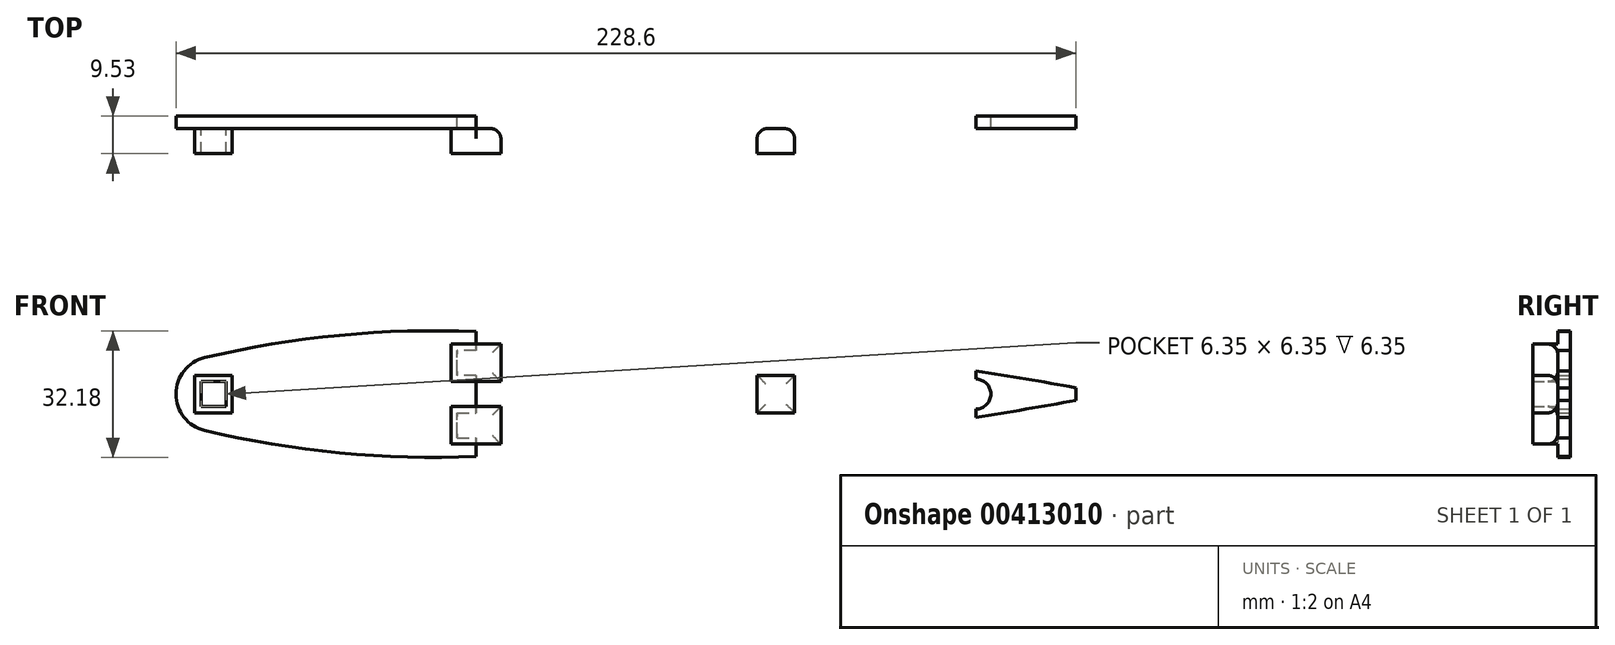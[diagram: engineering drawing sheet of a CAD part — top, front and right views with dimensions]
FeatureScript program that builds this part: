
annotation { "Feature Type Name" : "Feature", "Feature Type Description" : "" }
export const myFeature = defineFeature(function(context is Context, id is Id, definition is map)
    precondition{}
    {
        {
            var Q0;
            Q0=qCreatedBy(makeId("Front.planeOp"),FACE);
            var sketch = newSketch(context, id + "F0", { "sketchPlane" : qUnion([Q0])});
            skLineSegment(sketch, "E0", {"start": v(-94.05, 0) * mm, "end": v(-84.53, 0) * mm});
            skArc(sketch, "E1", {"start": v(-86.72, 9.27) * mm, "mid": v(-94.05, 0) * mm, "end": v(-86.72, -9.27) * mm});
            skLineSegment(sketch, "E2", {"start": v(-94.05, 0) * mm, "end": v(-17.85, 0) * mm});
            skLineSegment(sketch, "E3", {"start": v(-17.85, 0) * mm, "end": v(-17.85, 15.88) * mm});
            skLineSegment(sketch, "E4", {"start": v(-84.53, 0) * mm, "end": v(-84.53, 3.17) * mm});
            skLineSegment(sketch, "E5", {"start": v(-84.53, 0) * mm, "end": v(-84.53, -3.18) * mm});
            skLineSegment(sketch, "E6", {"start": v(-17.85, 0) * mm, "end": v(-17.85, -15.88) * mm});
            skLineSegment(sketch, "E7", {"start": v(134.55, 0) * mm, "end": v(134.55, 1.6) * mm});
            skLineSegment(sketch, "E8", {"start": v(134.55, 0) * mm, "end": v(134.55, -1.6) * mm});
            skArc(sketch, "E9", {"start": v(134.55, 1.6) * mm, "mid": v(58.66, 12.12) * mm, "end": v(-17.85, 15.88) * mm});
            skArc(sketch, "E10", {"start": v(-17.85, -15.87) * mm, "mid": v(58.66, -12.12) * mm, "end": v(134.55, -1.6) * mm});
            skLineSegment(sketch, "E11.bottom", {"start": v(-81.35, -3.18) * mm, "end": v(-87.7, -3.18) * mm});
            skLineSegment(sketch, "E11.top", {"start": v(-81.35, 3.17) * mm, "end": v(-87.7, 3.17) * mm});
            skLineSegment(sketch, "E11.left", {"start": v(-81.35, -3.18) * mm, "end": v(-81.35, 3.17) * mm});
            skLineSegment(sketch, "E11.right", {"start": v(-87.7, -3.18) * mm, "end": v(-87.7, 3.17) * mm});
            skLineSegment(sketch, "E12.bottom", {"start": v(-13.09, 4.76) * mm, "end": v(-22.61, 4.76) * mm});
            skLineSegment(sketch, "E12.top", {"start": v(-13.09, 11.11) * mm, "end": v(-22.61, 11.11) * mm});
            skLineSegment(sketch, "E12.left", {"start": v(-13.09, 4.76) * mm, "end": v(-13.09, 11.11) * mm});
            skLineSegment(sketch, "E12.right", {"start": v(-22.61, 4.76) * mm, "end": v(-22.61, 11.11) * mm});
            skPoint(sketch, "E12.middle", {"position": v(-17.85, 7.94) * mm});
            skLineSegment(sketch, "E13.bottom", {"start": v(-22.61, -11.11) * mm, "end": v(-13.09, -11.11) * mm});
            skLineSegment(sketch, "E13.top", {"start": v(-22.61, -4.76) * mm, "end": v(-13.09, -4.76) * mm});
            skLineSegment(sketch, "E13.left", {"start": v(-22.61, -11.11) * mm, "end": v(-22.61, -4.76) * mm});
            skLineSegment(sketch, "E13.right", {"start": v(-13.09, -11.11) * mm, "end": v(-13.09, -4.76) * mm});
            skPoint(sketch, "E13.middle", {"position": v(-17.85, -7.94) * mm});
            skLineSegment(sketch, "E14", {"start": v(-17.85, 0) * mm, "end": v(58.35, 0) * mm});
            skLineSegment(sketch, "E15.bottom", {"start": v(61.52, 3.17) * mm, "end": v(55.17, 3.17) * mm});
            skLineSegment(sketch, "E15.top", {"start": v(61.52, -3.17) * mm, "end": v(55.17, -3.17) * mm});
            skLineSegment(sketch, "E15.left", {"start": v(61.52, 3.17) * mm, "end": v(61.52, -3.17) * mm});
            skLineSegment(sketch, "E15.right", {"start": v(55.17, 3.17) * mm, "end": v(55.17, -3.17) * mm});
            skPoint(sketch, "E15.middle", {"position": v(58.35, 0) * mm});
            skArc(sketch, "E16", {"start": v(-17.85, 15.88) * mm, "mid": v(-52.51, 14.93) * mm, "end": v(-86.72, 9.27) * mm});
            skArc(sketch, "E17", {"start": v(-86.72, -9.27) * mm, "mid": v(-52.51, -14.93) * mm, "end": v(-17.85, -15.88) * mm});
            skLineSegment(sketch, "E18", {"start": v(134.55, 0) * mm, "end": v(109.15, 0) * mm});
            skLineSegment(sketch, "E19", {"start": v(109.15, 0) * mm, "end": v(109.15, -5.89) * mm});
            skLineSegment(sketch, "E20", {"start": v(109.15, 0) * mm, "end": v(109.15, 5.89) * mm});
            skCircle(sketch, "E21", {"center": v(109.15, 0) * mm, "radius": 3.81 * mm});
            skSolve(sketch);
        }
        {
            var Q0;
            {var subQ0=sQuery(id+"F0.wireOp",EDGE,"E12.right");Q0=makeQuery(id+"F0.imprint","IMPRINT",FACE,{"disambiguationData":[TD([[makeQuery(id+"F0.imprint","IMPRINT",EDGE,{"derivedFrom":subQ0}),1.0]])]});}
            var Q1;
            {var subQ8=sQuery(id+"F0.wireOp",EDGE,"E13.left");Q1=makeQuery(id+"F0.imprint","IMPRINT",FACE,{"disambiguationData":[TD([[makeQuery(id+"F0.imprint","IMPRINT",EDGE,{"derivedFrom":subQ8}),1.0]])]});}
            var Q2;
            {var subQ0=sQuery(id+"F0.wireOp",EDGE,"E12.left");Q2=makeQuery(id+"F0.imprint","IMPRINT",FACE,{"disambiguationData":[TD([[makeQuery(id+"F0.imprint","IMPRINT",EDGE,{"derivedFrom":subQ0}),-1.0]])]});}
            var Q3;
            {var subQ1=sQuery(id+"F0.wireOp",EDGE,"E8");Q3=makeQuery(id+"F0.imprint","IMPRINT",FACE,{"disambiguationData":[TD([[makeQuery(id+"F0.imprint","IMPRINT",EDGE,{"derivedFrom":subQ1}),-1.0]])]});}
            var Q4;
            {var subQ6=sQuery(id+"F0.wireOp",EDGE,"E7");Q4=makeQuery(id+"F0.imprint","IMPRINT",FACE,{"disambiguationData":[TD([[makeQuery(id+"F0.imprint","IMPRINT",EDGE,{"derivedFrom":subQ6}),1.0]])]});}
            extrude(context, id + "F1", {"entities" : qUnion([Q0, Q1, Q2, Q3, Q4]), "depth" : 3.17 * mm});
        }
        {
            var Q0;
            Q0=makeQuery(id+"F1.opExtrude","CAP_FACE",FACE,{"disambiguationData":[OSD([sQuery(id+"F0.wireOp",EDGE,"E1"),sQuery(id+"F0.wireOp",EDGE,"E7"),sQuery(id+"F0.wireOp",EDGE,"E8"),sQuery(id+"F0.wireOp",EDGE,"E9"),sQuery(id+"F0.wireOp",EDGE,"E10"),sQuery(id+"F0.wireOp",EDGE,"E11.bottom"),sQuery(id+"F0.wireOp",EDGE,"E11.top"),sQuery(id+"F0.wireOp",EDGE,"E11.left"),sQuery(id+"F0.wireOp",EDGE,"E11.right"),sQuery(id+"F0.wireOp",EDGE,"E12.bottom"),sQuery(id+"F0.wireOp",EDGE,"E12.top"),sQuery(id+"F0.wireOp",EDGE,"E12.left"),sQuery(id+"F0.wireOp",EDGE,"E12.right"),sQuery(id+"F0.wireOp",EDGE,"E13.bottom"),sQuery(id+"F0.wireOp",EDGE,"E13.top"),sQuery(id+"F0.wireOp",EDGE,"E13.left"),sQuery(id+"F0.wireOp",EDGE,"E13.right"),sQuery(id+"F0.wireOp",EDGE,"E15.bottom"),sQuery(id+"F0.wireOp",EDGE,"E15.top"),sQuery(id+"F0.wireOp",EDGE,"E15.left"),sQuery(id+"F0.wireOp",EDGE,"E15.right"),sQuery(id+"F0.wireOp",EDGE,"E16"),sQuery(id+"F0.wireOp",EDGE,"E17"),sQuery(id+"F0.wireOp",EDGE,"E21")])],"isStart":false});
            var sketch = newSketch(context, id + "F2", { "sketchPlane" : qUnion([Q0])});
            skLineSegment(sketch, "E22.bottom", {"start": v(-79.76, 4.76) * mm, "end": v(-89.29, 4.76) * mm});
            skLineSegment(sketch, "E22.top", {"start": v(-79.76, -4.76) * mm, "end": v(-89.29, -4.76) * mm});
            skLineSegment(sketch, "E22.left", {"start": v(-79.76, 4.76) * mm, "end": v(-79.76, -4.76) * mm});
            skLineSegment(sketch, "E22.right", {"start": v(-89.29, 4.76) * mm, "end": v(-89.29, -4.76) * mm});
            skPoint(sketch, "E22.middle", {"position": v(-84.53, 0) * mm});
            skLineSegment(sketch, "E23", {"start": v(-22.61, 11.11) * mm, "end": v(-13.09, 4.76) * mm});
            skLineSegment(sketch, "E24", {"start": v(-22.61, -4.76) * mm, "end": v(-13.09, -11.11) * mm});
            skLineSegment(sketch, "E25", {"start": v(55.17, 3.17) * mm, "end": v(61.52, -3.17) * mm});
            skLineSegment(sketch, "E26.bottom", {"start": v(-24.2, 12.7) * mm, "end": v(-11.5, 12.7) * mm});
            skLineSegment(sketch, "E26.top", {"start": v(-24.2, 3.18) * mm, "end": v(-11.5, 3.18) * mm});
            skLineSegment(sketch, "E26.left", {"start": v(-24.2, 12.7) * mm, "end": v(-24.2, 3.18) * mm});
            skLineSegment(sketch, "E26.right", {"start": v(-11.5, 12.7) * mm, "end": v(-11.5, 3.18) * mm});
            skPoint(sketch, "E26.middle", {"position": v(-17.85, 7.94) * mm});
            skLineSegment(sketch, "E27.bottom", {"start": v(-24.2, -3.18) * mm, "end": v(-11.5, -3.18) * mm});
            skLineSegment(sketch, "E27.top", {"start": v(-24.2, -12.7) * mm, "end": v(-11.5, -12.7) * mm});
            skLineSegment(sketch, "E27.left", {"start": v(-24.2, -3.18) * mm, "end": v(-24.2, -12.7) * mm});
            skLineSegment(sketch, "E27.right", {"start": v(-11.5, -3.18) * mm, "end": v(-11.5, -12.7) * mm});
            skPoint(sketch, "E27.middle", {"position": v(-17.85, -7.94) * mm});
            skLineSegment(sketch, "E28.bottom", {"start": v(53.59, 4.76) * mm, "end": v(63.11, 4.76) * mm});
            skLineSegment(sketch, "E28.top", {"start": v(53.59, -4.76) * mm, "end": v(63.11, -4.76) * mm});
            skLineSegment(sketch, "E28.left", {"start": v(53.59, 4.76) * mm, "end": v(53.59, -4.76) * mm});
            skLineSegment(sketch, "E28.right", {"start": v(63.11, 4.76) * mm, "end": v(63.11, -4.76) * mm});
            skPoint(sketch, "E28.middle", {"position": v(58.35, 0) * mm});
            skSolve(sketch);
        }
        {
            var Q0;
            Q0=makeQuery(id+"F2.imprint","IMPRINT",FACE,{"disambiguationData":[TD([[makeQuery(id+"F2.imprint","IMPRINT",EDGE,{"derivedFrom":sQuery(id+"F2.wireOp",EDGE,"E22.bottom")}),1.0]])]});
            var Q1;
            Q1=makeQuery(id+"F2.imprint","IMPRINT",FACE,{"disambiguationData":[TD([[makeQuery(id+"F2.imprint","IMPRINT",EDGE,{"derivedFrom":sQuery(id+"F2.wireOp",EDGE,"E26.bottom")}),-1.0]])]});
            var Q2;
            Q2=makeQuery(id+"F2.imprint","IMPRINT",FACE,{"disambiguationData":[TD([[makeQuery(id+"F2.imprint","IMPRINT",EDGE,{"derivedFrom":sQuery(id+"F2.wireOp",EDGE,"E27.bottom")}),-1.0]])]});
            var Q3;
            Q3=makeQuery(id+"F2.imprint","IMPRINT",FACE,{"disambiguationData":[TD([[makeQuery(id+"F2.imprint","IMPRINT",EDGE,{"derivedFrom":sQuery(id+"F2.wireOp",EDGE,"E28.bottom")}),-1.0]])]});
            extrude(context, id + "F3", {"entities" : qUnion([Q0, Q1, Q2, Q3]), "operationType" : NewBodyOperationType.ADD, "depth" : 6.35 * mm});
        }
        {
            var Q0;
            Q0=makeQuery(id+"F3.opExtrude","CAP_EDGE",EDGE,{"disambiguationData":[OSD([sQuery(id+"F2.wireOp",EDGE,"E22.top")])],"isStart":true});
            var Q1;
            Q1=makeQuery(id+"F3.opExtrude","CAP_EDGE",EDGE,{"disambiguationData":[OSD([sQuery(id+"F2.wireOp",EDGE,"E22.right")])],"isStart":true});
            var Q2;
            Q2=makeQuery(id+"F3.opExtrude","CAP_EDGE",EDGE,{"disambiguationData":[OSD([sQuery(id+"F2.wireOp",EDGE,"E22.bottom")])],"isStart":true});
            var Q3;
            Q3=makeQuery(id+"F3.opExtrude","CAP_EDGE",EDGE,{"disambiguationData":[OSD([sQuery(id+"F2.wireOp",EDGE,"E22.left")])],"isStart":true});
            var Q4;
            Q4=makeQuery(id+"F3.opExtrude","CAP_EDGE",EDGE,{"disambiguationData":[OSD([sQuery(id+"F2.wireOp",EDGE,"E26.right")])],"isStart":true});
            var Q5;
            Q5=makeQuery(id+"F3.opExtrude","CAP_EDGE",EDGE,{"disambiguationData":[OSD([sQuery(id+"F2.wireOp",EDGE,"E26.bottom")])],"isStart":true});
            var Q6;
            Q6=makeQuery(id+"F3.opExtrude","CAP_EDGE",EDGE,{"disambiguationData":[OSD([sQuery(id+"F2.wireOp",EDGE,"E27.bottom")])],"isStart":true});
            var Q7;
            Q7=makeQuery(id+"F3.opExtrude","CAP_EDGE",EDGE,{"disambiguationData":[OSD([sQuery(id+"F2.wireOp",EDGE,"E27.right")])],"isStart":true});
            var Q8;
            Q8=makeQuery(id+"F3.opExtrude","CAP_EDGE",EDGE,{"disambiguationData":[OSD([sQuery(id+"F2.wireOp",EDGE,"E28.bottom")])],"isStart":true});
            var Q9;
            Q9=makeQuery(id+"F3.opExtrude","CAP_EDGE",EDGE,{"disambiguationData":[OSD([sQuery(id+"F2.wireOp",EDGE,"E28.right")])],"isStart":true});
            var Q10;
            Q10=makeQuery(id+"F3.opExtrude","CAP_EDGE",EDGE,{"disambiguationData":[OSD([sQuery(id+"F2.wireOp",EDGE,"E28.left")])],"isStart":true});
            var Q11;
            Q11=makeQuery(id+"F3.opExtrude","CAP_EDGE",EDGE,{"disambiguationData":[OSD([sQuery(id+"F2.wireOp",EDGE,"E28.top")])],"isStart":true});
            var Q12;
            Q12=makeQuery(id+"F3.opExtrude","CAP_EDGE",EDGE,{"disambiguationData":[OSD([sQuery(id+"F2.wireOp",EDGE,"E26.left")])],"isStart":true});
            var Q13;
            Q13=makeQuery(id+"F3.opExtrude","CAP_EDGE",EDGE,{"disambiguationData":[OSD([sQuery(id+"F2.wireOp",EDGE,"E26.top")])],"isStart":true});
            var Q14;
            Q14=makeQuery(id+"F3.opExtrude","CAP_EDGE",EDGE,{"disambiguationData":[OSD([sQuery(id+"F2.wireOp",EDGE,"E27.left")])],"isStart":true});
            var Q15;
            Q15=makeQuery(id+"F3.opExtrude","CAP_EDGE",EDGE,{"disambiguationData":[OSD([sQuery(id+"F2.wireOp",EDGE,"E27.top")])],"isStart":true});
            fillet(context, id + "F4", {"entities" : qUnion([Q0, Q1, Q2, Q3, Q4, Q5, Q6, Q7, Q8, Q9, Q10, Q11, Q12, Q13, Q14, Q15]), "radius" : 2.54 * mm, "tangentPropagation" : true, "allowEdgeOverflow" : false});
        }
        {
            var Q0;
            Q0=makeQuery(id+"F1.opExtrude","CAP_FACE",FACE,{"disambiguationData":[OSD([sQuery(id+"F0.wireOp",EDGE,"E1"),sQuery(id+"F0.wireOp",EDGE,"E7"),sQuery(id+"F0.wireOp",EDGE,"E8"),sQuery(id+"F0.wireOp",EDGE,"E9"),sQuery(id+"F0.wireOp",EDGE,"E10"),sQuery(id+"F0.wireOp",EDGE,"E11.bottom"),sQuery(id+"F0.wireOp",EDGE,"E11.top"),sQuery(id+"F0.wireOp",EDGE,"E11.left"),sQuery(id+"F0.wireOp",EDGE,"E11.right"),sQuery(id+"F0.wireOp",EDGE,"E12.bottom"),sQuery(id+"F0.wireOp",EDGE,"E12.top"),sQuery(id+"F0.wireOp",EDGE,"E12.left"),sQuery(id+"F0.wireOp",EDGE,"E12.right"),sQuery(id+"F0.wireOp",EDGE,"E13.bottom"),sQuery(id+"F0.wireOp",EDGE,"E13.top"),sQuery(id+"F0.wireOp",EDGE,"E13.left"),sQuery(id+"F0.wireOp",EDGE,"E13.right"),sQuery(id+"F0.wireOp",EDGE,"E15.bottom"),sQuery(id+"F0.wireOp",EDGE,"E15.top"),sQuery(id+"F0.wireOp",EDGE,"E15.left"),sQuery(id+"F0.wireOp",EDGE,"E15.right"),sQuery(id+"F0.wireOp",EDGE,"E16"),sQuery(id+"F0.wireOp",EDGE,"E17"),sQuery(id+"F0.wireOp",EDGE,"E21")])],"isStart":true});
            var sketch = newSketch(context, id + "F5", { "sketchPlane" : qUnion([Q0])});
            skSolve(sketch);
        }
        {
            var Q0;
            Q0=makeQuery(id+"F5.imprint","IMPRINT",FACE,{"disambiguationData":[TD([[makeQuery(id+"F5.imprint","IMPRINT",EDGE,{"derivedFrom":makeQuery(id+"F1.opExtrude","CAP_EDGE",EDGE,{"disambiguationData":[OSD([sQuery(id+"F0.wireOp",EDGE,"E15.bottom")])],"isStart":true})}),-1.0]])]});
            var Q1;
            Q1=makeQuery(id+"F5.imprint","IMPRINT",FACE,{"disambiguationData":[TD([[makeQuery(id+"F5.imprint","IMPRINT",EDGE,{"derivedFrom":makeQuery(id+"F1.opExtrude","CAP_EDGE",EDGE,{"disambiguationData":[OSD([sQuery(id+"F0.wireOp",EDGE,"E12.bottom")])],"isStart":true})}),1.0]])]});
            var Q2;
            Q2=makeQuery(id+"F5.imprint","IMPRINT",FACE,{"disambiguationData":[TD([[makeQuery(id+"F5.imprint","IMPRINT",EDGE,{"derivedFrom":makeQuery(id+"F1.opExtrude","CAP_EDGE",EDGE,{"disambiguationData":[OSD([sQuery(id+"F0.wireOp",EDGE,"E13.bottom")])],"isStart":true})}),-1.0]])]});
            var Q3;
            Q3=makeQuery(id+"F5.imprint","IMPRINT",FACE,{"disambiguationData":[TD([[makeQuery(id+"F5.imprint","IMPRINT",EDGE,{"derivedFrom":makeQuery(id+"F1.opExtrude","CAP_EDGE",EDGE,{"disambiguationData":[OSD([sQuery(id+"F0.wireOp",EDGE,"E11.bottom")])],"isStart":true})}),1.0]])]});
            extrude(context, id + "F6", {"entities" : qUnion([Q0, Q1, Q2, Q3]), "operationType" : NewBodyOperationType.ADD, "oppositeDirection" : true, "depth" : 3.17 * mm});
        }
    });
